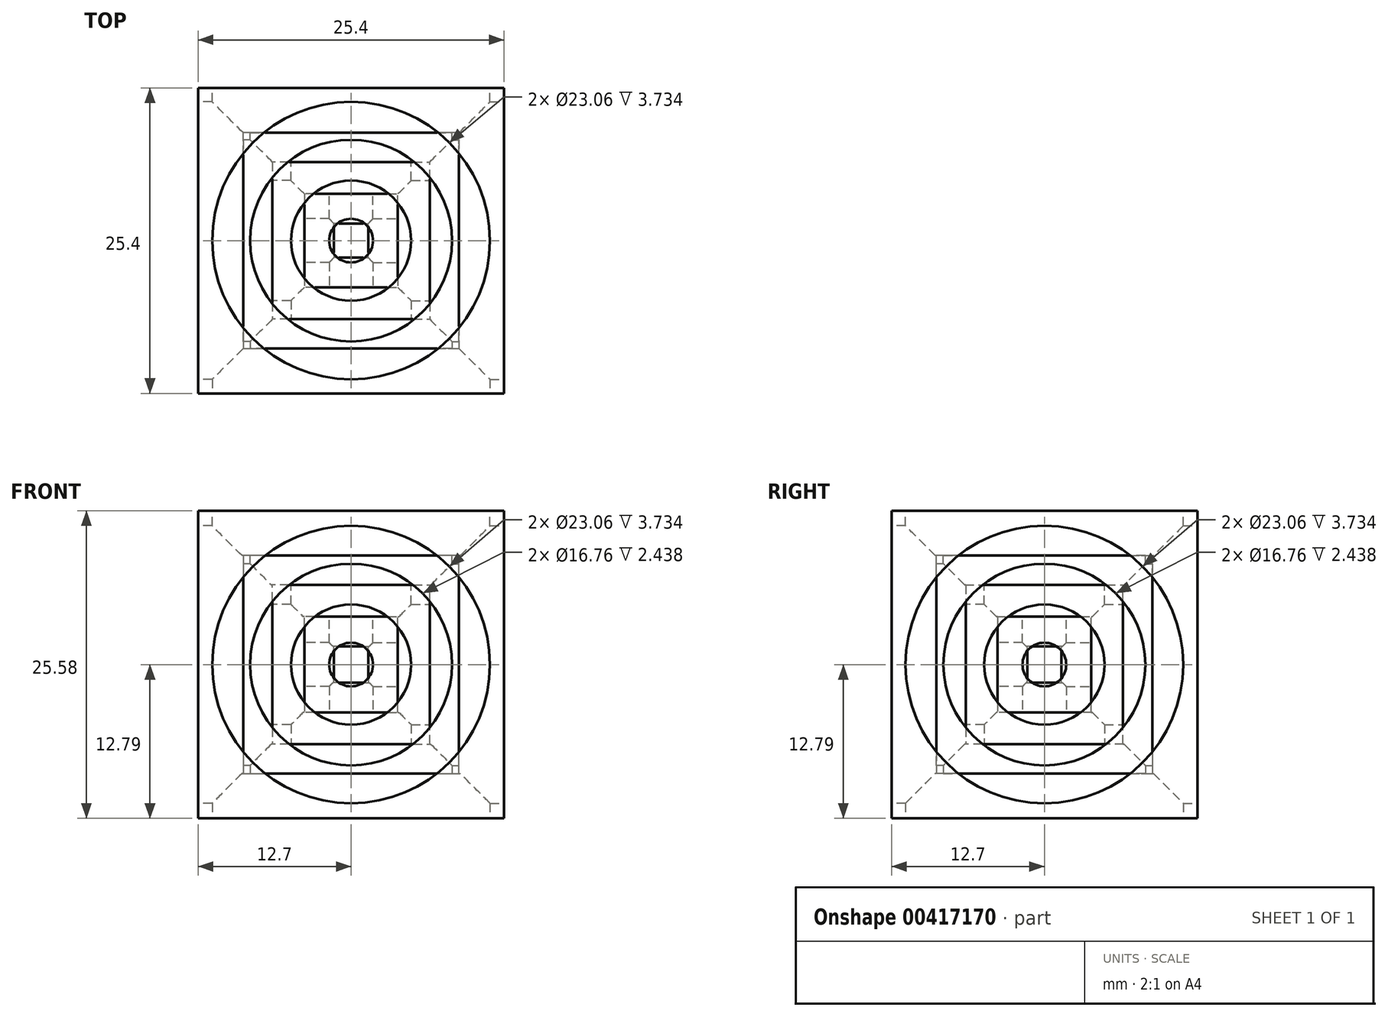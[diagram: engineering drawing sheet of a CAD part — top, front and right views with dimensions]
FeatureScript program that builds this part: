
annotation { "Feature Type Name" : "Feature", "Feature Type Description" : "" }
export const myFeature = defineFeature(function(context is Context, id is Id, definition is map)
    precondition{}
    {
        {
            var Q0;
            Q0=qCreatedBy(makeId("Front.planeOp"),FACE);
            var sketch = newSketch(context, id + "F0", { "sketchPlane" : qUnion([Q0])});
            skLineSegment(sketch, "E0.bottom", {"start": v(12.7, 12.8) * mm, "end": v(-12.7, 12.8) * mm});
            skLineSegment(sketch, "E0.top", {"start": v(12.7, -12.8) * mm, "end": v(-12.7, -12.8) * mm});
            skLineSegment(sketch, "E0.left", {"start": v(12.7, 12.8) * mm, "end": v(12.7, -12.8) * mm});
            skLineSegment(sketch, "E0.right", {"start": v(-12.7, 12.8) * mm, "end": v(-12.7, -12.8) * mm});
            skPoint(sketch, "E0.middle", {"position": v(0, 0) * mm});
            skSolve(sketch);
        }
        {
            var Q0;
            Q0=qCreatedBy(makeId("Front.planeOp"),FACE);
            var sketch = newSketch(context, id + "F1", { "sketchPlane" : qUnion([Q0])});
            skCircle(sketch, "E1", {"center": v(0, 0) * mm, "radius": 11.53 * mm});
            skCircle(sketch, "E2", {"center": v(0, 0) * mm, "radius": 5 * mm});
            skCircle(sketch, "E3", {"center": v(0, 0) * mm, "radius": 8.38 * mm});
            skCircle(sketch, "E4", {"center": v(0, 0) * mm, "radius": 1.82 * mm});
            skSolve(sketch);
        }
        {
            var Q0;
            Q0 = qSketchRegion(id + "F0", true);
            extrude(context, id + "F2", {"entities" : qUnion([Q0]), "oppositeDirection" : true, "depth" : 25.4 * mm});
        }
        {
            var Q0;
            Q0=makeQuery(id+"F1.imprint","IMPRINT",FACE,{"disambiguationData":[TD([[makeQuery(id+"F1.imprint","IMPRINT",EDGE,{"derivedFrom":sQuery(id+"F1.wireOp",EDGE,"E4")}),1.0]])]});
            extrude(context, id + "F3", {"entities" : qUnion([Q0]), "operationType" : NewBodyOperationType.REMOVE, "oppositeDirection" : true, "depth" : 11.28 * mm});
        }
        {
            var Q0;
            Q0=makeQuery(id+"F1.imprint","IMPRINT",FACE,{"disambiguationData":[TD([[makeQuery(id+"F1.imprint","IMPRINT",EDGE,{"derivedFrom":sQuery(id+"F1.wireOp",EDGE,"E1")}),1.0]])]});
            var Q1;
            Q1=sQuery(id+"F1.wireOp",EDGE,"E1");
            extrude(context, id + "F4", {"entities" : qUnion([Q0]), "operationType" : NewBodyOperationType.REMOVE, "surfaceEntities" : qUnion([Q1]), "oppositeDirection" : true, "depth" : 3.73 * mm});
        }
        {
            var Q0;
            Q0=makeQuery(id+"F1.imprint","IMPRINT",FACE,{"disambiguationData":[TD([[makeQuery(id+"F1.imprint","IMPRINT",EDGE,{"derivedFrom":sQuery(id+"F1.wireOp",EDGE,"E2")}),1.0]])]});
            var Q1;
            Q1=sQuery(id+"F1.wireOp",EDGE,"E2");
            extrude(context, id + "F5", {"entities" : qUnion([Q0]), "operationType" : NewBodyOperationType.REMOVE, "surfaceEntities" : qUnion([Q1]), "oppositeDirection" : true, "depth" : 8.8 * mm});
        }
        {
            var Q0;
            Q0=makeQuery(id+"F1.imprint","IMPRINT",FACE,{"disambiguationData":[TD([[makeQuery(id+"F1.imprint","IMPRINT",EDGE,{"derivedFrom":sQuery(id+"F1.wireOp",EDGE,"E2")}),-1.0]])]});
            extrude(context, id + "F6", {"entities" : qUnion([Q0]), "operationType" : NewBodyOperationType.REMOVE, "oppositeDirection" : true, "depth" : 6.17 * mm});
        }
        {
            var Q0;
            Q0=makeQuery(id+"F2.opExtrude","SWEPT_FACE",FACE,{"disambiguationData":[OSD([sQuery(id+"F0.wireOp",EDGE,"E0.right")])]});
            var sketch = newSketch(context, id + "F7", { "sketchPlane" : qUnion([Q0])});
            skCircle(sketch, "E5", {"center": v(-12.7, 0) * mm, "radius": 11.53 * mm});
            skCircle(sketch, "E6", {"center": v(-12.7, 0) * mm, "radius": 5 * mm});
            skCircle(sketch, "E7", {"center": v(-12.7, 0) * mm, "radius": 8.38 * mm});
            skCircle(sketch, "E8", {"center": v(-12.7, 0) * mm, "radius": 1.82 * mm});
            skSolve(sketch);
        }
        {
            var Q0;
            Q0=makeQuery(id+"F2.opExtrude","SWEPT_FACE",FACE,{"disambiguationData":[OSD([sQuery(id+"F0.wireOp",EDGE,"E0.top")])]});
            var sketch = newSketch(context, id + "F8", { "sketchPlane" : qUnion([Q0])});
            skCircle(sketch, "E9", {"center": v(0, -12.7) * mm, "radius": 11.53 * mm});
            skCircle(sketch, "E10", {"center": v(0, -12.7) * mm, "radius": 5 * mm});
            skCircle(sketch, "E11", {"center": v(0, -12.7) * mm, "radius": 8.38 * mm});
            skCircle(sketch, "E12", {"center": v(0, -12.7) * mm, "radius": 1.82 * mm});
            skSolve(sketch);
        }
        {
            var Q0;
            Q0=makeQuery(id+"F2.opExtrude","SWEPT_FACE",FACE,{"disambiguationData":[OSD([sQuery(id+"F0.wireOp",EDGE,"E0.bottom")])]});
            var sketch = newSketch(context, id + "F9", { "sketchPlane" : qUnion([Q0])});
            skCircle(sketch, "E13", {"center": v(0, 12.7) * mm, "radius": 11.53 * mm});
            skCircle(sketch, "E14", {"center": v(0, 12.7) * mm, "radius": 5 * mm});
            skCircle(sketch, "E15", {"center": v(0, 12.7) * mm, "radius": 8.38 * mm});
            skCircle(sketch, "E16", {"center": v(0, 12.7) * mm, "radius": 1.82 * mm});
            skSolve(sketch);
        }
        {
            var Q0;
            Q0=makeQuery(id+"F2.opExtrude","SWEPT_FACE",FACE,{"disambiguationData":[OSD([sQuery(id+"F0.wireOp",EDGE,"E0.left")])]});
            var sketch = newSketch(context, id + "F10", { "sketchPlane" : qUnion([Q0])});
            skCircle(sketch, "E17", {"center": v(12.7, 0) * mm, "radius": 11.53 * mm});
            skCircle(sketch, "E18", {"center": v(12.7, 0) * mm, "radius": 5 * mm});
            skCircle(sketch, "E19", {"center": v(12.7, 0) * mm, "radius": 8.38 * mm});
            skCircle(sketch, "E20", {"center": v(12.7, 0) * mm, "radius": 1.82 * mm});
            skSolve(sketch);
        }
        {
            var Q0;
            Q0=makeQuery(id+"F2.opExtrude","CAP_FACE",FACE,{"disambiguationData":[OSD([sQuery(id+"F0.wireOp",EDGE,"E0.bottom"),sQuery(id+"F0.wireOp",EDGE,"E0.top"),sQuery(id+"F0.wireOp",EDGE,"E0.left"),sQuery(id+"F0.wireOp",EDGE,"E0.right")])],"isStart":false});
            var sketch = newSketch(context, id + "F11", { "sketchPlane" : qUnion([Q0])});
            skCircle(sketch, "E21", {"center": v(0, 0) * mm, "radius": 11.53 * mm});
            skCircle(sketch, "E22", {"center": v(0, 0) * mm, "radius": 5 * mm});
            skCircle(sketch, "E23", {"center": v(0, 0) * mm, "radius": 8.38 * mm});
            skCircle(sketch, "E24", {"center": v(0, 0) * mm, "radius": 1.82 * mm});
            skSolve(sketch);
        }
        {
            var Q0;
            Q0=makeQuery(id+"F7.imprint","IMPRINT",FACE,{"disambiguationData":[TD([[makeQuery(id+"F7.imprint","IMPRINT",EDGE,{"derivedFrom":sQuery(id+"F7.wireOp",EDGE,"E8")}),1.0]])]});
            var Q1;
            Q1=sQuery(id+"F7.wireOp",EDGE,"E8");
            extrude(context, id + "F12", {"entities" : qUnion([Q0]), "operationType" : NewBodyOperationType.REMOVE, "surfaceEntities" : qUnion([Q1]), "oppositeDirection" : true, "depth" : 11.28 * mm});
        }
        {
            var Q0;
            Q0=makeQuery(id+"F8.imprint","IMPRINT",FACE,{"disambiguationData":[TD([[makeQuery(id+"F8.imprint","IMPRINT",EDGE,{"derivedFrom":sQuery(id+"F8.wireOp",EDGE,"E12")}),1.0]])]});
            var Q1;
            Q1=sQuery(id+"F8.wireOp",EDGE,"E12");
            extrude(context, id + "F13", {"entities" : qUnion([Q0]), "operationType" : NewBodyOperationType.REMOVE, "surfaceEntities" : qUnion([Q1]), "oppositeDirection" : true, "depth" : 11.28 * mm});
        }
        {
            var Q0;
            Q0=makeQuery(id+"F9.imprint","IMPRINT",FACE,{"disambiguationData":[TD([[makeQuery(id+"F9.imprint","IMPRINT",EDGE,{"derivedFrom":sQuery(id+"F9.wireOp",EDGE,"E16")}),1.0]])]});
            var Q1;
            Q1=sQuery(id+"F9.wireOp",EDGE,"E16");
            extrude(context, id + "F14", {"entities" : qUnion([Q0]), "operationType" : NewBodyOperationType.REMOVE, "surfaceEntities" : qUnion([Q1]), "oppositeDirection" : true, "depth" : 11.28 * mm});
        }
        {
            var Q0;
            Q0=makeQuery(id+"F11.imprint","IMPRINT",FACE,{"disambiguationData":[TD([[makeQuery(id+"F11.imprint","IMPRINT",EDGE,{"derivedFrom":sQuery(id+"F11.wireOp",EDGE,"E24")}),1.0]])]});
            var Q1;
            Q1=sQuery(id+"F11.wireOp",EDGE,"E24");
            extrude(context, id + "F15", {"entities" : qUnion([Q0]), "operationType" : NewBodyOperationType.REMOVE, "surfaceEntities" : qUnion([Q1]), "oppositeDirection" : true, "depth" : 11.28 * mm});
        }
        {
            var Q0;
            Q0=makeQuery(id+"F10.imprint","IMPRINT",FACE,{"disambiguationData":[TD([[makeQuery(id+"F10.imprint","IMPRINT",EDGE,{"derivedFrom":sQuery(id+"F10.wireOp",EDGE,"E20")}),1.0]])]});
            var Q1;
            Q1=sQuery(id+"F10.wireOp",EDGE,"E20");
            extrude(context, id + "F16", {"entities" : qUnion([Q0]), "operationType" : NewBodyOperationType.REMOVE, "surfaceEntities" : qUnion([Q1]), "oppositeDirection" : true, "depth" : 11.28 * mm});
        }
        {
            var Q0;
            Q0=makeQuery(id+"F9.imprint","IMPRINT",FACE,{"disambiguationData":[TD([[makeQuery(id+"F9.imprint","IMPRINT",EDGE,{"derivedFrom":sQuery(id+"F9.wireOp",EDGE,"E14")}),1.0]])]});
            var Q1;
            Q1=sQuery(id+"F9.wireOp",EDGE,"E14");
            extrude(context, id + "F17", {"entities" : qUnion([Q0]), "operationType" : NewBodyOperationType.REMOVE, "surfaceEntities" : qUnion([Q1]), "oppositeDirection" : true, "depth" : 8.8 * mm});
        }
        {
            var Q0;
            Q0=makeQuery(id+"F11.imprint","IMPRINT",FACE,{"disambiguationData":[TD([[makeQuery(id+"F11.imprint","IMPRINT",EDGE,{"derivedFrom":sQuery(id+"F11.wireOp",EDGE,"E22")}),1.0]])]});
            var Q1;
            Q1=sQuery(id+"F11.wireOp",EDGE,"E22");
            extrude(context, id + "F18", {"entities" : qUnion([Q0]), "operationType" : NewBodyOperationType.REMOVE, "surfaceEntities" : qUnion([Q1]), "oppositeDirection" : true, "depth" : 8.8 * mm});
        }
        {
            var Q0;
            Q0=makeQuery(id+"F11.imprint","IMPRINT",FACE,{"disambiguationData":[TD([[makeQuery(id+"F11.imprint","IMPRINT",EDGE,{"derivedFrom":sQuery(id+"F11.wireOp",EDGE,"E22")}),-1.0]])]});
            var Q1;
            Q1=sQuery(id+"F11.wireOp",EDGE,"E23");
            extrude(context, id + "F19", {"entities" : qUnion([Q0]), "operationType" : NewBodyOperationType.REMOVE, "surfaceEntities" : qUnion([Q1]), "oppositeDirection" : true, "depth" : 6.17 * mm});
        }
        {
            var Q0;
            Q0=makeQuery(id+"F11.imprint","IMPRINT",FACE,{"disambiguationData":[TD([[makeQuery(id+"F11.imprint","IMPRINT",EDGE,{"derivedFrom":sQuery(id+"F11.wireOp",EDGE,"E21")}),1.0]])]});
            var Q1;
            Q1=sQuery(id+"F11.wireOp",EDGE,"E21");
            extrude(context, id + "F20", {"entities" : qUnion([Q0]), "operationType" : NewBodyOperationType.REMOVE, "surfaceEntities" : qUnion([Q1]), "oppositeDirection" : true, "depth" : 3.73 * mm});
        }
        {
            var Q0;
            Q0=makeQuery(id+"F9.imprint","IMPRINT",FACE,{"disambiguationData":[TD([[makeQuery(id+"F9.imprint","IMPRINT",EDGE,{"derivedFrom":sQuery(id+"F9.wireOp",EDGE,"E14")}),1.0]])]});
            var Q1;
            Q1=sQuery(id+"F9.wireOp",EDGE,"E14");
            extrude(context, id + "F21", {"entities" : qUnion([Q0]), "operationType" : NewBodyOperationType.REMOVE, "surfaceEntities" : qUnion([Q1]), "oppositeDirection" : true, "depth" : 8.8 * mm});
        }
        {
            var Q0;
            Q0=makeQuery(id+"F9.imprint","IMPRINT",FACE,{"disambiguationData":[TD([[makeQuery(id+"F9.imprint","IMPRINT",EDGE,{"derivedFrom":sQuery(id+"F9.wireOp",EDGE,"E14")}),-1.0]])]});
            var Q1;
            Q1=sQuery(id+"F9.wireOp",EDGE,"E15");
            extrude(context, id + "F22", {"entities" : qUnion([Q0]), "operationType" : NewBodyOperationType.REMOVE, "surfaceEntities" : qUnion([Q1]), "oppositeDirection" : true, "depth" : 6.17 * mm});
        }
        {
            var Q0;
            Q0=makeQuery(id+"F9.imprint","IMPRINT",FACE,{"disambiguationData":[TD([[makeQuery(id+"F9.imprint","IMPRINT",EDGE,{"derivedFrom":sQuery(id+"F9.wireOp",EDGE,"E13")}),1.0]])]});
            var Q1;
            Q1=sQuery(id+"F9.wireOp",EDGE,"E13");
            extrude(context, id + "F23", {"entities" : qUnion([Q0]), "operationType" : NewBodyOperationType.REMOVE, "surfaceEntities" : qUnion([Q1]), "oppositeDirection" : true, "depth" : 3.73 * mm});
        }
        {
            var Q0;
            Q0=makeQuery(id+"F10.imprint","IMPRINT",FACE,{"disambiguationData":[TD([[makeQuery(id+"F10.imprint","IMPRINT",EDGE,{"derivedFrom":sQuery(id+"F10.wireOp",EDGE,"E18")}),1.0]])]});
            var Q1;
            Q1=sQuery(id+"F10.wireOp",EDGE,"E18");
            extrude(context, id + "F24", {"entities" : qUnion([Q0]), "operationType" : NewBodyOperationType.REMOVE, "surfaceEntities" : qUnion([Q1]), "oppositeDirection" : true, "depth" : 8.8 * mm});
        }
        {
            var Q0;
            Q0=makeQuery(id+"F10.imprint","IMPRINT",FACE,{"disambiguationData":[TD([[makeQuery(id+"F10.imprint","IMPRINT",EDGE,{"derivedFrom":sQuery(id+"F10.wireOp",EDGE,"E18")}),-1.0]])]});
            var Q1;
            Q1=sQuery(id+"F10.wireOp",EDGE,"E19");
            extrude(context, id + "F25", {"entities" : qUnion([Q0]), "operationType" : NewBodyOperationType.REMOVE, "surfaceEntities" : qUnion([Q1]), "oppositeDirection" : true, "depth" : 6.17 * mm});
        }
        {
            var Q0;
            Q0=makeQuery(id+"F10.imprint","IMPRINT",FACE,{"disambiguationData":[TD([[makeQuery(id+"F10.imprint","IMPRINT",EDGE,{"derivedFrom":sQuery(id+"F10.wireOp",EDGE,"E17")}),1.0]])]});
            var Q1;
            Q1=sQuery(id+"F10.wireOp",EDGE,"E17");
            extrude(context, id + "F26", {"entities" : qUnion([Q0]), "operationType" : NewBodyOperationType.REMOVE, "surfaceEntities" : qUnion([Q1]), "oppositeDirection" : true, "depth" : 3.73 * mm});
        }
        {
            var Q0;
            Q0=makeQuery(id+"F8.imprint","IMPRINT",FACE,{"disambiguationData":[TD([[makeQuery(id+"F8.imprint","IMPRINT",EDGE,{"derivedFrom":sQuery(id+"F8.wireOp",EDGE,"E10")}),1.0]])]});
            var Q1;
            Q1=sQuery(id+"F8.wireOp",EDGE,"E10");
            var Q2;
            Q2=sQuery(id+"F9.wireOp",EDGE,"E15");
            var Q3;
            Q3=sQuery(id+"F8.wireOp",EDGE,"E11");
            extrude(context, id + "F27", {"entities" : qUnion([Q0]), "operationType" : NewBodyOperationType.REMOVE, "surfaceEntities" : qUnion([Q1, Q2, Q3]), "oppositeDirection" : true, "depth" : 8.8 * mm});
        }
        {
            var Q0;
            Q0=makeQuery(id+"F8.imprint","IMPRINT",FACE,{"disambiguationData":[TD([[makeQuery(id+"F8.imprint","IMPRINT",EDGE,{"derivedFrom":sQuery(id+"F8.wireOp",EDGE,"E10")}),-1.0]])]});
            var Q1;
            Q1=sQuery(id+"F8.wireOp",EDGE,"E11");
            extrude(context, id + "F28", {"entities" : qUnion([Q0]), "operationType" : NewBodyOperationType.REMOVE, "surfaceEntities" : qUnion([Q1]), "oppositeDirection" : true, "depth" : 6.17 * mm});
        }
        {
            var Q0;
            Q0=makeQuery(id+"F7.imprint","IMPRINT",FACE,{"disambiguationData":[TD([[makeQuery(id+"F7.imprint","IMPRINT",EDGE,{"derivedFrom":sQuery(id+"F7.wireOp",EDGE,"E6")}),1.0]])]});
            var Q1;
            Q1=sQuery(id+"F7.wireOp",EDGE,"E6");
            extrude(context, id + "F29", {"entities" : qUnion([Q0]), "operationType" : NewBodyOperationType.REMOVE, "surfaceEntities" : qUnion([Q1]), "oppositeDirection" : true, "depth" : 8.8 * mm});
        }
        {
            var Q0;
            Q0=makeQuery(id+"F7.imprint","IMPRINT",FACE,{"disambiguationData":[TD([[makeQuery(id+"F7.imprint","IMPRINT",EDGE,{"derivedFrom":sQuery(id+"F7.wireOp",EDGE,"E6")}),-1.0]])]});
            var Q1;
            Q1=sQuery(id+"F7.wireOp",EDGE,"E7");
            extrude(context, id + "F30", {"entities" : qUnion([Q0]), "operationType" : NewBodyOperationType.REMOVE, "surfaceEntities" : qUnion([Q1]), "oppositeDirection" : true, "depth" : 6.17 * mm});
        }
        {
            var Q0;
            Q0=makeQuery(id+"F7.imprint","IMPRINT",FACE,{"disambiguationData":[TD([[makeQuery(id+"F7.imprint","IMPRINT",EDGE,{"derivedFrom":sQuery(id+"F7.wireOp",EDGE,"E5")}),1.0]])]});
            var Q1;
            Q1=sQuery(id+"F7.wireOp",EDGE,"E5");
            extrude(context, id + "F31", {"entities" : qUnion([Q0]), "operationType" : NewBodyOperationType.REMOVE, "surfaceEntities" : qUnion([Q1]), "oppositeDirection" : true, "depth" : 3.73 * mm});
        }
        {
            var Q0;
            Q0=makeQuery(id+"F8.imprint","IMPRINT",FACE,{"disambiguationData":[TD([[makeQuery(id+"F8.imprint","IMPRINT",EDGE,{"derivedFrom":sQuery(id+"F8.wireOp",EDGE,"E9")}),1.0]])]});
            var Q1;
            Q1=sQuery(id+"F8.wireOp",EDGE,"E9");
            extrude(context, id + "F32", {"entities" : qUnion([Q0]), "operationType" : NewBodyOperationType.REMOVE, "surfaceEntities" : qUnion([Q1]), "oppositeDirection" : true, "depth" : 3.73 * mm});
        }
    });
